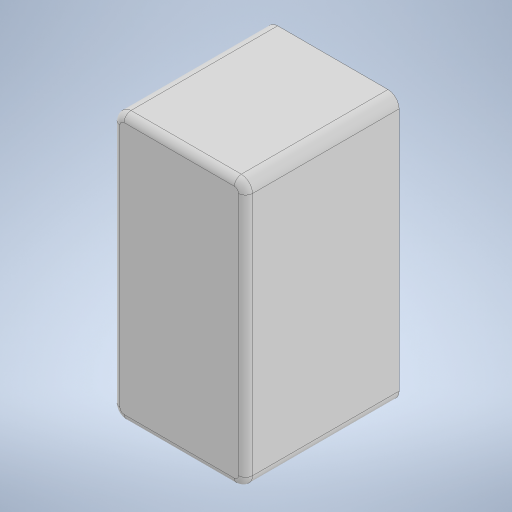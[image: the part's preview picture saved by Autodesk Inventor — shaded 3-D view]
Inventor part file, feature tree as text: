
AUTODESK INVENTOR PART (.ipt)
format: ipt  version: 2024 (Build 280153000, 153)  size: 291,328 bytes
history: native  units: mm
features: sketch x9, extrude x7, fillet x2, hole x2, other x1
ambient origin geometry x8: Origin, YZ Plane, XZ Plane, XY Plane, X Axis, Y Axis, Z Axis, Center Point
bodies: Body1 (feature_tree)
feature tree (21):
  other  "Těleso1"
  extrude  "Vysunutí1"  Depth=191.0mm
  extrude  "Vysunutí2"  Depth=95.0mm
  extrude  "Vysunutí3"  Depth=110.0mm TaperAngle=0.0deg
  extrude  "Vysunutí4"  Depth=85.0mm
  extrude  "Vysunutí6"  Depth=47.5mm
  fillet  "Zaoblení1"  Radius=85.0mm
  fillet  "Zaoblení2"  Radius=30.0mm
  extrude  "Vysunutí7"  Depth=85.0mm
  extrude  "Vysunutí8"  Depth=47.5mm
  hole  "Díra1"  [1 undecoded]
  hole  "Díra2"  [1 undecoded]
  sketch  "Náčrt1"
  sketch  "Náčrt2"
  sketch  "Náčrt3"
  sketch  "Náčrt4"
  sketch  "Náčrt6"
  sketch  "Náčrt7"
  sketch  "Náčrt8"
  sketch  "Náčrt9"
  sketch  "Náčrt10"
note: 2 required parameter values undecoded (feature->parameter linkage not recoverable at this tier; creation-order binding heuristic only, values carry confidence <= 0.55)
